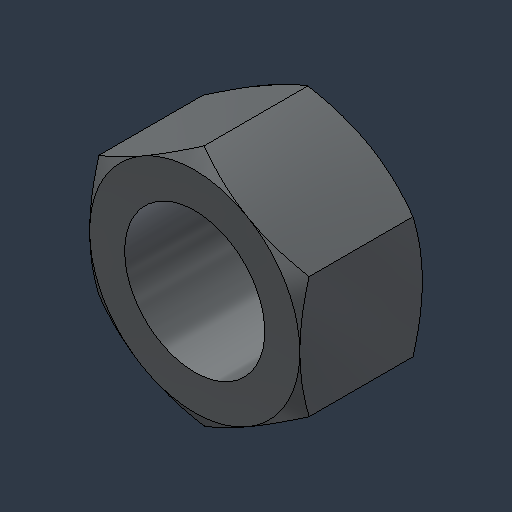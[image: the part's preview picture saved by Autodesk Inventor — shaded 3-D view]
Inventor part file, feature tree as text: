
AUTODESK INVENTOR PART (.ipt)
format: ipt  version: 2024.3 (Build 283343000, 343)  size: 123,392 bytes
history: native  units: mm (DEFAULTED — no unit token found)
features: mirror x1
ambient origin geometry x8: Origin, YZ Plane, XZ Plane, XY Plane, X Axis, Y Axis, Z Axis, Center Point
bodies: Solid1 (feature_tree)
feature tree (1):
  mirror  "Mirror1"
